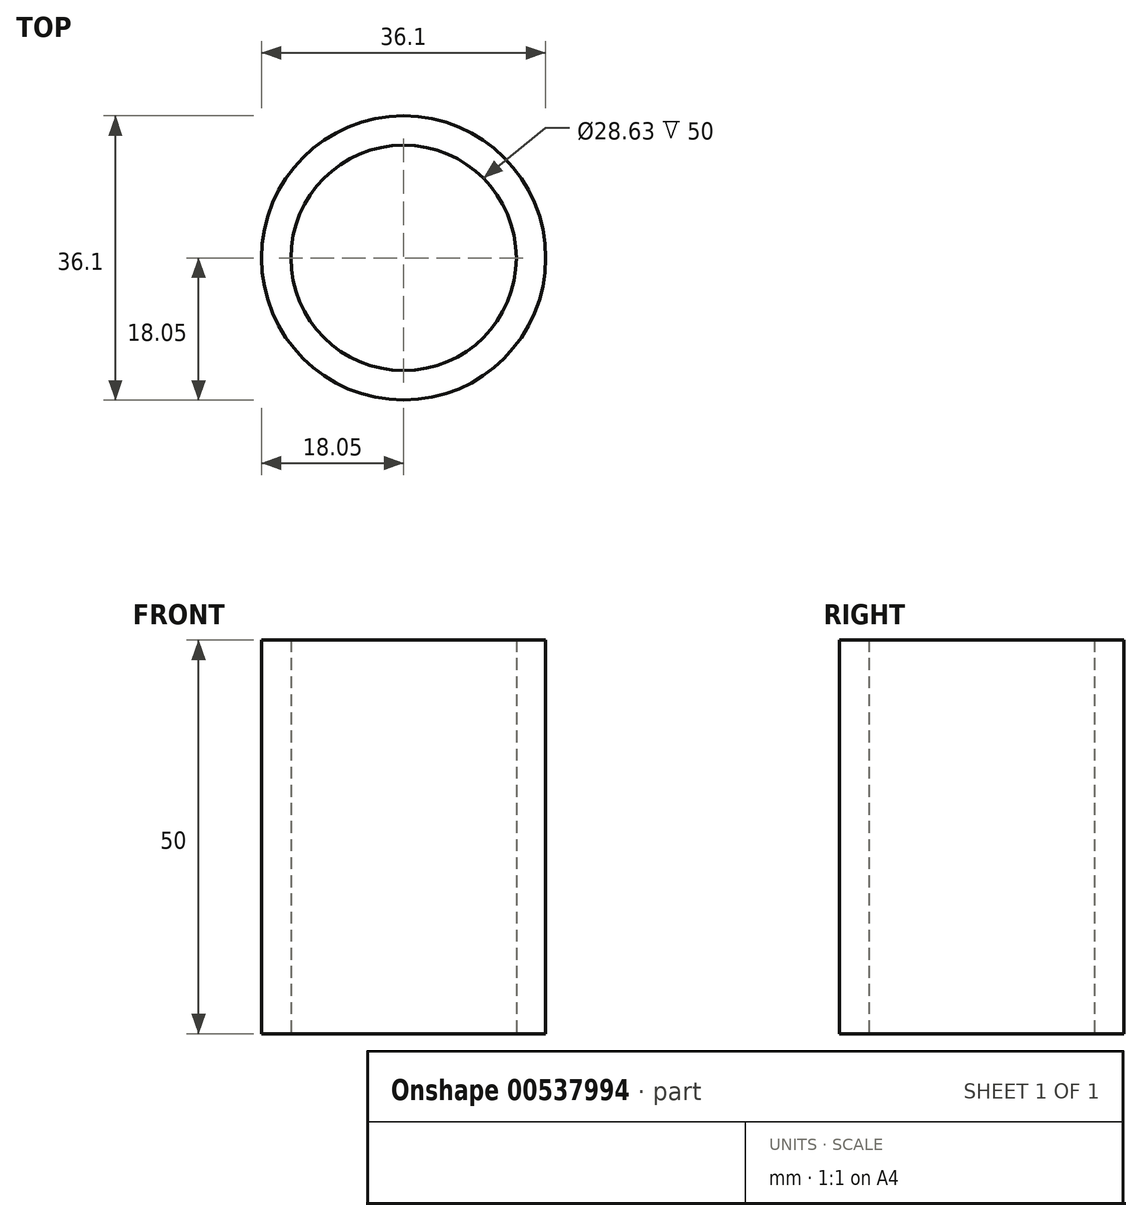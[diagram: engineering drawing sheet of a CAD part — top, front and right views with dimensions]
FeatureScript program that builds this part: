
annotation { "Feature Type Name" : "Feature", "Feature Type Description" : "" }
export const myFeature = defineFeature(function(context is Context, id is Id, definition is map)
    precondition{}
    {
        {
            var Q0;
            Q0=qCreatedBy(makeId("Top.planeOp"),FACE);
            var sketch = newSketch(context, id + "F0", { "sketchPlane" : qUnion([Q0])});
            skCircle(sketch, "E0", {"center": v(0, 0) * mm, "radius": 18.05 * mm});
            skCircle(sketch, "E1", {"center": v(0, 0) * mm, "radius": 14.32 * mm});
            skSolve(sketch);
        }
        {
            var Q0;
            Q0=makeQuery(id+"F0.imprint","IMPRINT",FACE,{"disambiguationData":[TD([[makeQuery(id+"F0.imprint","IMPRINT",EDGE,{"derivedFrom":sQuery(id+"F0.wireOp",EDGE,"E0")}),1.0]])]});
            extrude(context, id + "F1", {"entities" : qUnion([Q0]), "depth" : 50 * mm, "offsetDistance" : 25 * mm});
        }
    });
